# Revit family: BOS-Pendeltuerzarge-Pe-STW_Familie
name_source: partatom
category: Türen
revit_build: Autodesk Revit 2017 (Build: 20160225_1515(x64)
units: mm (PartAtom-declared; Revit-internal decimal feet)

## family parameters
Basisbauteil = Wand
Beim Laden mit Abzugskörper schneiden = Nein
Gemeinsam genutzt = Nein
Immer vertikal = Ja
Raumberechnungspunkt = Ja

## types (1)
- Pe
    BBL1 Bandbezugslinie   Hinge Position 1 = 241 mm  [stored 0.790682 ft]
    BE max. = 100 mm  [stored 0.328084 ft]
    Bandgröße = 39
    Bauelement = BOS Stahlzarge
    Beschreibung = Pendeltürzarge für Ständerwerk
    Blechstärke = 1.5 mm  [stored 0.00492126 ft]
    Breite = 0 mm  [stored 0 ft]
    Dicke = 0 mm  [stored 0 ft]
    Drehpunkt Warnung sichtbar = Ja
    Drehpunktabstand (L) horizontal = -8 mm  [stored -0.0262467 ft]
    Drehpunktreferenz horizontal = 500 mm  [stored 1.64042 ft]
    Funktion = Innen
    GT max. = 650 mm  [stored 2.13255 ft]
    Hersteller = BOS GmbH Best Of Steel, Lütkenfelde 4, D-48282 Emsdetten
    Info-Texte sichtbar = Ja
    Information in English = Nein
    MW min. = 100 mm  [stored 0.328084 ft]
    Material = grundiert, feuerverzinktes Feinblech nach DIN EN 10143
    Material - Bänder = <Nach Kategorie>
    Material - Glasleisten = <Nach Kategorie>
    Material - Türblatt = <Nach Kategorie>
    Material - Türgriff = <Nach Kategorie>
    Material - Verglasung = Glas
    Material - Zarge = <Nach Kategorie>
    Modell = Pe
    PLDB max. = 999 mm  [stored 3.27756 ft]
    PLDB min. = 598 mm  [stored 1.96194 ft]
    PLDH max. = 2814 mm  [stored 9.23228 ft]
    PLDH min. = 1861 mm  [stored 6.10564 ft]
    Pe = Ja
    Putzwinkel max. = 28 mm  [stored 0.0918635 ft]
    Putzwinkel min. = 10 mm  [stored 0.0328084 ft]
    Rohbaubreite = 0 mm  [stored 0 ft]
    Rohbauhöhe = 0 mm  [stored 0 ft]
    Spiegel hinten max. = 80 mm  [stored 0.262467 ft]
    Spiegel hinten min. = 30 mm  [stored 0.0984252 ft]
    Spiegel innen max. = 20 mm  [stored 0.0656168 ft]
    Spiegel innen min. = 20 mm  [stored 0.0656168 ft]
    Spiegel vorne max. = 80 mm  [stored 0.262467 ft]
    Spiegel vorne min. = 30 mm  [stored 0.0984252 ft]
    Stumpf = Ja
    Technische Infos rund um die Stahlzarge = www.BestOfSteel.de/tools-downloads/technische-infos-rund-um-die-stahlzarge/
    Typenbild = <Keine Auswahl>
    Türblattabstand umlaufend = 7 mm  [stored 0.0229659 ft]
    Türblattstärke = 40 mm  [stored 0.131234 ft]
    Türblattversatz  horizontal = -1 mm  [stored -0.00328084 ft]
    URL = www.BestOfSteel.de/stahlzargen/zargen-fuer-drehfluegeltueren/pendeltuerzargen/
    Öffnungswinkel max. = 90.00°
    Öffnungswinkel min. = 0.00°

note: [stored X ft] marks values corroborated as IEEE doubles in the binary element streams (Revit-internal decimal feet)
